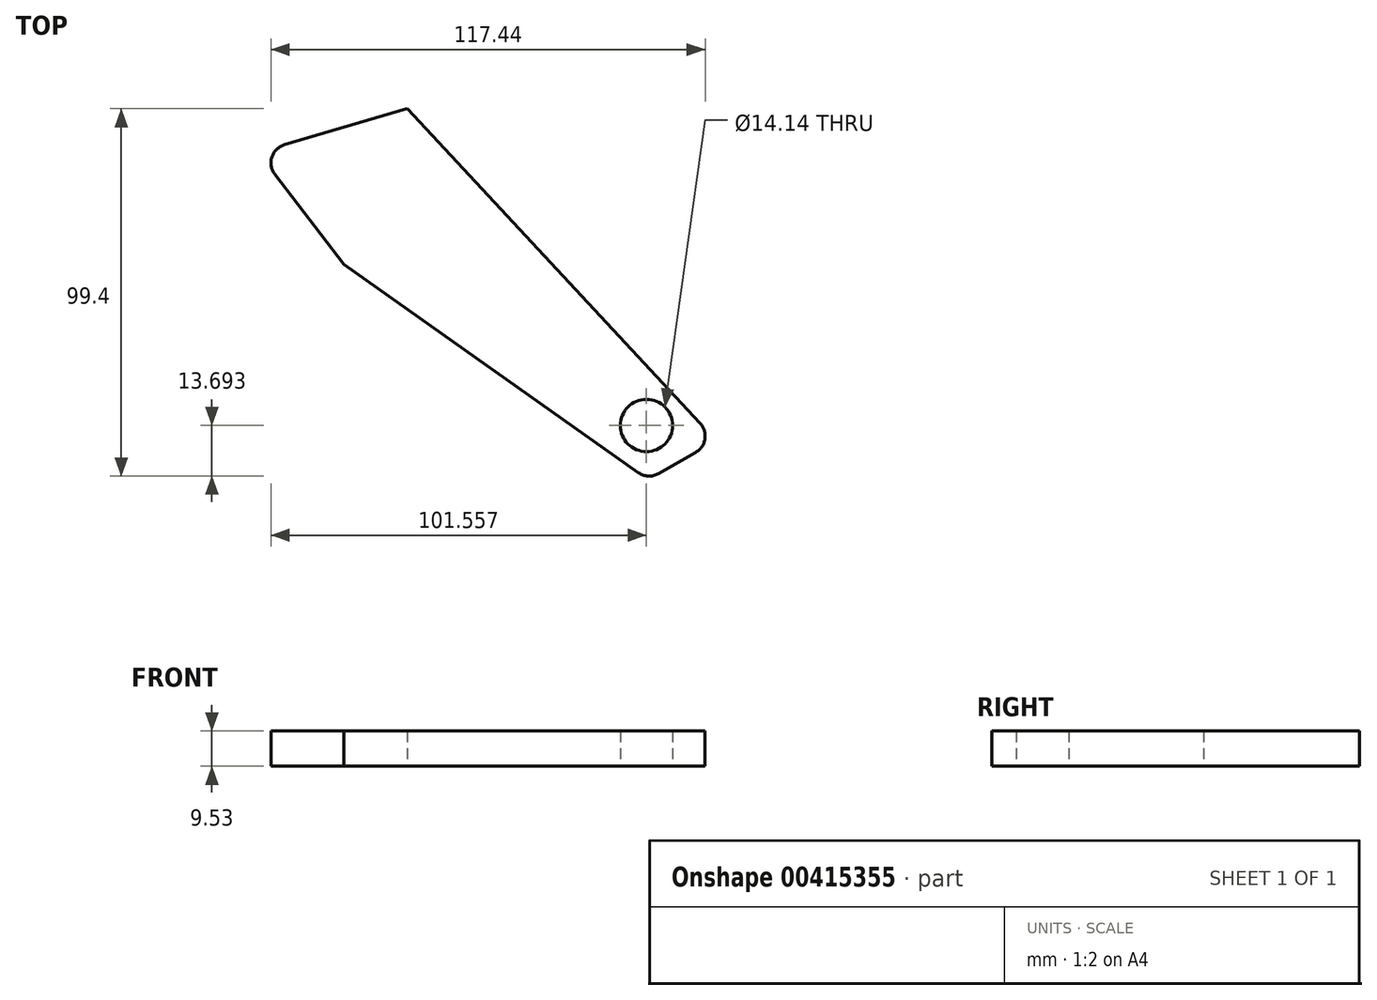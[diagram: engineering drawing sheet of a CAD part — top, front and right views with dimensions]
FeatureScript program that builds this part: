
annotation { "Feature Type Name" : "Feature", "Feature Type Description" : "" }
export const myFeature = defineFeature(function(context is Context, id is Id, definition is map)
    precondition{}
    {
        {
            var Q0;
            Q0=qCreatedBy(makeId("Top.planeOp"),FACE);
            var sketch = newSketch(context, id + "F0", { "sketchPlane" : qUnion([Q0])});
            skLineSegment(sketch, "E0", {"start": v(55.04, -31.63) * mm, "end": v(-28.5, 58.2) * mm});
            skLineSegment(sketch, "E1", {"start": v(-68.84, 46.34) * mm, "end": v(-28.5, 58.2) * mm});
            skLineSegment(sketch, "E2", {"start": v(-68.84, 46.34) * mm, "end": v(-45.74, 16.05) * mm});
            skLineSegment(sketch, "E3", {"start": v(-45.74, 16.05) * mm, "end": v(36.6, -42.14) * mm});
            skLineSegment(sketch, "E4", {"start": v(36.6, -42.14) * mm, "end": v(55.04, -31.63) * mm});
            skSolve(sketch);
        }
        {
            var Q0;
            Q0=qSketchRegion(id+"F0",true);
            extrude(context, id + "F1", {"entities" : qUnion([Q0]), "depth" : 9.52 * mm});
        }
        {
            var Q0;
            Q0=makeQuery(id+"F1.opExtrude","SWEPT_EDGE",EDGE,{"disambiguationData":[OSD([sQuery(id+"F0.wireOp",EDGE,"E1"),sQuery(id+"F0.wireOp",EDGE,"E2")])]});
            fillet(context, id + "F2", {"entities" : qUnion([Q0]), "radius" : 5.08 * mm, "tangentPropagation" : true, "allowEdgeOverflow" : false});
        }
        {
            var Q0;
            Q0=makeQuery(id+"F1.opExtrude","SWEPT_EDGE",EDGE,{"disambiguationData":[OSD([sQuery(id+"F0.wireOp",EDGE,"E3"),sQuery(id+"F0.wireOp",EDGE,"E4")])]});
            fillet(context, id + "F3", {"entities" : qUnion([Q0]), "radius" : 5.08 * mm, "tangentPropagation" : true, "allowEdgeOverflow" : false});
        }
        {
            var Q0;
            Q0=makeQuery(id+"F1.opExtrude","SWEPT_EDGE",EDGE,{"disambiguationData":[OSD([sQuery(id+"F0.wireOp",EDGE,"E0"),sQuery(id+"F0.wireOp",EDGE,"E4")])]});
            fillet(context, id + "F4", {"entities" : qUnion([Q0]), "radius" : 5.08 * mm, "tangentPropagation" : true, "allowEdgeOverflow" : false});
        }
        {
            var Q0;
            Q0=makeQuery(id+"F1.opExtrude","CAP_FACE",FACE,{"disambiguationData":[OSD([sQuery(id+"F0.wireOp",EDGE,"E0"),sQuery(id+"F0.wireOp",EDGE,"E1"),sQuery(id+"F0.wireOp",EDGE,"E2"),sQuery(id+"F0.wireOp",EDGE,"E3"),sQuery(id+"F0.wireOp",EDGE,"E4")])],"isStart":true});
            var sketch = newSketch(context, id + "F5", { "sketchPlane" : qUnion([Q0])});
            skCircle(sketch, "E5", {"center": v(36.16, 27.52) * mm, "radius": 7.07 * mm});
            skSolve(sketch);
        }
        {
            var Q0;
            Q0=makeQuery(id+"F5.imprint","IMPRINT",FACE,{"disambiguationData":[TD([[makeQuery(id+"F5.imprint","IMPRINT",EDGE,{"derivedFrom":sQuery(id+"F5.wireOp",EDGE,"E5")}),1.0]])]});
            extrude(context, id + "F6", {"entities" : qUnion([Q0]), "operationType" : NewBodyOperationType.REMOVE, "oppositeDirection" : true, "depth" : 75.62 * mm});
        }
    });
